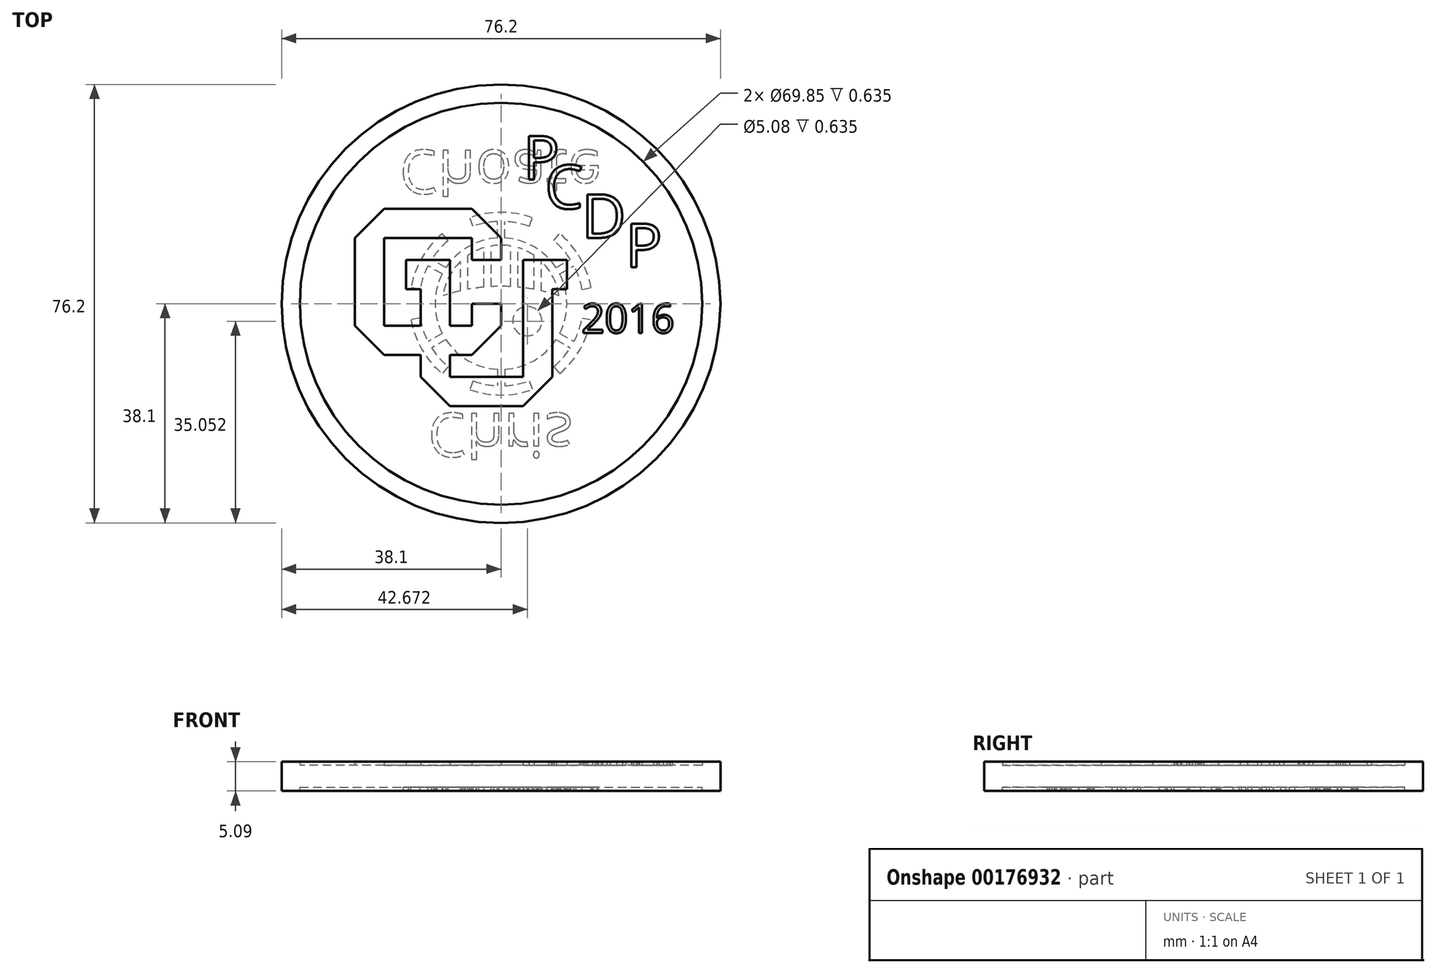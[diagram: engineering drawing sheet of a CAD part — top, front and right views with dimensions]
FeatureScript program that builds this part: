
annotation { "Feature Type Name" : "Feature", "Feature Type Description" : "" }
export const myFeature = defineFeature(function(context is Context, id is Id, definition is map)
    precondition{}
    {
        {
            var Q0;
            Q0=qCreatedBy(makeId("Top.planeOp"),FACE);
            var sketch = newSketch(context, id + "F0", { "sketchPlane" : qUnion([Q0])});
            skCircle(sketch, "E0", {"center": v(0, 0) * mm, "radius": 38.1 * mm});
            skSolve(sketch);
        }
        {
            var Q0;
            Q0=makeQuery(id+"F0.imprint","IMPRINT",FACE,{"disambiguationData":[TD([[makeQuery(id+"F0.imprint","IMPRINT",EDGE,{"derivedFrom":sQuery(id+"F0.wireOp",EDGE,"E0")}),1.0]])]});
            extrude(context, id + "F1", {"entities" : qUnion([Q0]), "depth" : 3.8 * mm});
        }
        {
            var Q0;
            Q0=makeQuery(id+"F1.opExtrude","CAP_FACE",FACE,{"disambiguationData":[OSD([sQuery(id+"F0.wireOp",EDGE,"E0")])],"isStart":false});
            var sketch = newSketch(context, id + "F2", { "sketchPlane" : qUnion([Q0])});
            skLineSegment(sketch, "E1", {"start": v(0, 0) * mm, "end": v(0, -3.81) * mm});
            skLineSegment(sketch, "E2", {"start": v(0, -3.81) * mm, "end": v(-5.08, -8.9) * mm});
            skLineSegment(sketch, "E3", {"start": v(-5.08, -8.9) * mm, "end": v(-8.9, -8.9) * mm});
            skLineSegment(sketch, "E4", {"start": v(-20.32, -8.9) * mm, "end": v(-25.4, -3.81) * mm});
            skLineSegment(sketch, "E5", {"start": v(-25.4, -3.81) * mm, "end": v(-25.4, 11.43) * mm});
            skLineSegment(sketch, "E6", {"start": v(-25.4, 11.43) * mm, "end": v(-20.32, 16.5) * mm});
            skLineSegment(sketch, "E7", {"start": v(-20.32, 16.51) * mm, "end": v(-5.08, 16.51) * mm});
            skLineSegment(sketch, "E8", {"start": v(-5.08, 16.51) * mm, "end": v(0, 11.43) * mm});
            skLineSegment(sketch, "E9", {"start": v(0, 11.43) * mm, "end": v(0, 7.62) * mm});
            skLineSegment(sketch, "E10", {"start": v(0, 7.62) * mm, "end": v(-5.08, 7.62) * mm});
            skLineSegment(sketch, "E11", {"start": v(-5.08, 7.62) * mm, "end": v(-5.08, 11.43) * mm});
            skLineSegment(sketch, "E12", {"start": v(-5.08, 11.43) * mm, "end": v(-20.32, 11.43) * mm});
            skLineSegment(sketch, "E13", {"start": v(-20.32, 11.43) * mm, "end": v(-20.32, -3.81) * mm});
            skLineSegment(sketch, "E14", {"start": v(-20.32, -3.81) * mm, "end": v(-13.97, -3.81) * mm});
            skLineSegment(sketch, "E15", {"start": v(-5.08, -3.81) * mm, "end": v(-5.08, 0) * mm});
            skLineSegment(sketch, "E16", {"start": v(-5.08, 0) * mm, "end": v(0, 0) * mm});
            skLineSegment(sketch, "E17", {"start": v(-8.9, -3.81) * mm, "end": v(-8.9, 7.62) * mm});
            skLineSegment(sketch, "E18", {"start": v(-8.9, 7.62) * mm, "end": v(-16.5, 7.62) * mm});
            skLineSegment(sketch, "E19", {"start": v(-16.5, 7.62) * mm, "end": v(-16.5, 2.54) * mm});
            skLineSegment(sketch, "E20", {"start": v(-16.51, 2.54) * mm, "end": v(-13.97, 2.54) * mm});
            skLineSegment(sketch, "E21", {"start": v(-13.97, 2.54) * mm, "end": v(-13.97, -3.8) * mm});
            skLineSegment(sketch, "E22.trimOffspring", {"start": v(-8.9, -3.81) * mm, "end": v(-5.08, -3.81) * mm});
            skLineSegment(sketch, "E23", {"start": v(-13.97, -12.7) * mm, "end": v(-13.97, -8.9) * mm});
            skLineSegment(sketch, "E24", {"start": v(-13.97, -12.7) * mm, "end": v(-8.9, -17.78) * mm});
            skLineSegment(sketch, "E25", {"start": v(-8.9, -17.78) * mm, "end": v(3.8, -17.78) * mm});
            skLineSegment(sketch, "E26", {"start": v(3.8, -17.78) * mm, "end": v(8.89, -12.7) * mm});
            skLineSegment(sketch, "E27", {"start": v(8.89, -12.7) * mm, "end": v(8.9, 2.54) * mm});
            skLineSegment(sketch, "E28", {"start": v(8.9, 2.54) * mm, "end": v(11.43, 2.54) * mm});
            skLineSegment(sketch, "E29", {"start": v(11.43, 2.54) * mm, "end": v(11.43, 7.62) * mm});
            skLineSegment(sketch, "E30", {"start": v(11.43, 7.62) * mm, "end": v(3.8, 7.62) * mm});
            skLineSegment(sketch, "E31", {"start": v(3.8, 7.62) * mm, "end": v(3.8, -12.7) * mm});
            skLineSegment(sketch, "E32", {"start": v(3.8, -12.7) * mm, "end": v(-8.9, -12.7) * mm});
            skLineSegment(sketch, "E33", {"start": v(-8.9, -12.7) * mm, "end": v(-8.9, -8.9) * mm});
            skLineSegment(sketch, "E34.trimOffspring", {"start": v(-13.97, -8.9) * mm, "end": v(-20.32, -8.9) * mm});
            skCircle(sketch, "E35", {"center": v(0, 0) * mm, "radius": 38.1 * mm});
            skCircle(sketch, "E36.0", {"center": v(0, 0) * mm, "radius": 34.93 * mm});
            skText(sketch, "E37", { "text": "P\n", "fontName": "OpenSans-Regular.ttf"});
            skText(sketch, "E38", { "text": "C\n", "fontName": "OpenSans-Regular.ttf"});
            skText(sketch, "E39", { "text": "D\n", "fontName": "OpenSans-Regular.ttf"});
            skText(sketch, "E40", { "text": "P\n", "fontName": "OpenSans-Regular.ttf"});
            skText(sketch, "E41", { "text": "2016\n", "fontName": "OpenSans-Regular.ttf"});
            const initialGuessF2  = {"E37": [0.0038, 0.0216, 1, 0, 0.00762], "E38": [0.00762, 0.01651, 1, 0, 0.00762], "E39": [0.01397, 0.01143, 1, 0, 0.00762], "E40": [0.0216, 0.00635, 1, 0, 0.00762], "E41": [0.01397, -0.00508, 1, 0, 0.00508]};
            skSetInitialGuess(sketch, initialGuessF2);
            skSolve(sketch);
        }
        {
            var Q0;
            Q0 = qSketchRegion(id + "F2", true);
            var Q1;
            Q1=makeQuery(id+"F2.imprint","IMPRINT",FACE,{"disambiguationData":[TD([[makeQuery(id+"F2.imprint","IMPRINT",EDGE,{"derivedFrom":sQuery(id+"F2.wireOp",EDGE,"E37.sketch_text.stroke-0")}),-1.0]])]});
            var Q2;
            Q2=makeQuery(id+"F2.imprint","IMPRINT",FACE,{"disambiguationData":[TD([[makeQuery(id+"F2.imprint","IMPRINT",EDGE,{"derivedFrom":sQuery(id+"F2.wireOp",EDGE,"E38.sketch_text.stroke-0")}),-1.0]])]});
            var Q3;
            Q3=makeQuery(id+"F2.imprint","IMPRINT",FACE,{"disambiguationData":[TD([[makeQuery(id+"F2.imprint","IMPRINT",EDGE,{"derivedFrom":sQuery(id+"F2.wireOp",EDGE,"E39.sketch_text.stroke-0")}),-1.0]])]});
            var Q4;
            Q4=makeQuery(id+"F2.imprint","IMPRINT",FACE,{"disambiguationData":[TD([[makeQuery(id+"F2.imprint","IMPRINT",EDGE,{"derivedFrom":sQuery(id+"F2.wireOp",EDGE,"E40.sketch_text.stroke-0")}),-1.0]])]});
            var Q5;
            Q5=makeQuery(id+"F2.imprint","IMPRINT",FACE,{"disambiguationData":[TD([[makeQuery(id+"F2.imprint","IMPRINT",EDGE,{"derivedFrom":sQuery(id+"F2.wireOp",EDGE,"E1")}),-1.0]])]});
            var Q6;
            Q6=makeQuery(id+"F2.imprint","IMPRINT",FACE,{"disambiguationData":[TD([[makeQuery(id+"F2.imprint","IMPRINT",EDGE,{"derivedFrom":sQuery(id+"F2.wireOp",EDGE,"E41.sketch_text.stroke-0")}),-1.0]])]});
            var Q7;
            Q7=makeQuery(id+"F2.imprint","IMPRINT",FACE,{"disambiguationData":[TD([[makeQuery(id+"F2.imprint","IMPRINT",EDGE,{"derivedFrom":sQuery(id+"F2.wireOp",EDGE,"E41.sketch_text.stroke-20")}),-1.0]])]});
            var Q8;
            Q8=makeQuery(id+"F2.imprint","IMPRINT",FACE,{"disambiguationData":[TD([[makeQuery(id+"F2.imprint","IMPRINT",EDGE,{"derivedFrom":sQuery(id+"F2.wireOp",EDGE,"E41.sketch_text.stroke-36")}),-1.0]])]});
            var Q9;
            Q9=makeQuery(id+"F2.imprint","IMPRINT",FACE,{"disambiguationData":[TD([[makeQuery(id+"F2.imprint","IMPRINT",EDGE,{"derivedFrom":sQuery(id+"F2.wireOp",EDGE,"E41.sketch_text.stroke-45")}),-1.0]])]});
            extrude(context, id + "F3", {"entities" : qUnion([Q0, Q1, Q2, Q3, Q4, Q5, Q6, Q7, Q8, Q9]), "operationType" : NewBodyOperationType.ADD, "depth" : 0.64 * mm});
        }
        {
            var Q0;
            Q0=makeQuery(id+"F1.opExtrude","CAP_FACE",FACE,{"disambiguationData":[OSD([sQuery(id+"F0.wireOp",EDGE,"E0")])],"isStart":true});
            var sketch = newSketch(context, id + "F4", { "sketchPlane" : qUnion([Q0])});
            skCircle(sketch, "E42", {"center": v(0, 0) * mm, "radius": 38.1 * mm});
            skCircle(sketch, "E43", {"center": v(0, 0) * mm, "radius": 34.93 * mm});
            skText(sketch, "E44", { "text": "Chris\n", "fontName": "OpenSans-Regular.ttf"});
            skText(sketch, "E45", { "text": "Choate", "fontName": "OpenSans-Regular.ttf"});
            skArc(sketch, "E46", {"start": v(5.43, 14.92) * mm, "mid": v(0, 15.88) * mm, "end": v(-5.43, 14.92) * mm});
            skArc(sketch, "E47", {"start": v(4.89, 13.43) * mm, "mid": v(2.8, 14.01) * mm, "end": v(0.63, 14.27) * mm});
            skLineSegment(sketch, "E48", {"start": v(-4.89, 13.43) * mm, "end": v(-5.43, 14.92) * mm});
            skLineSegment(sketch, "E49.1.16.0", {"start": v(4.89, 13.43) * mm, "end": v(5.43, 14.92) * mm});
            skLineSegment(sketch, "E50", {"start": v(0.63, 11.41) * mm, "end": v(0.63, 14.27) * mm});
            skLineSegment(sketch, "E51", {"start": v(-0.64, 11.41) * mm, "end": v(-0.64, 14.27) * mm});
            skArc(sketch, "E52.trimOffspring", {"start": v(-0.64, 14.27) * mm, "mid": v(-2.8, 14.01) * mm, "end": v(-4.89, 13.43) * mm});
            skArc(sketch, "E53", {"start": v(-0.64, 11.41) * mm, "mid": v(-5.72, 9.9) * mm, "end": v(-9.57, 6.26) * mm});
            skLineSegment(sketch, "E54.1.0", {"start": v(-9.57, 6.26) * mm, "end": v(-12.04, 7.69) * mm});
            skLineSegment(sketch, "E54.1.1", {"start": v(-10.2, 5.16) * mm, "end": v(-12.68, 6.59) * mm});
            skArc(sketch, "E54.1.2", {"start": v(-12.68, 6.59) * mm, "mid": v(-13.53, 4.59) * mm, "end": v(-14.07, 2.48) * mm});
            skLineSegment(sketch, "E54.1.3", {"start": v(-14.07, 2.48) * mm, "end": v(-15.63, 2.76) * mm});
            skArc(sketch, "E54.1.4", {"start": v(-10.2, 12.16) * mm, "mid": v(-13.75, 7.94) * mm, "end": v(-15.63, 2.76) * mm});
            skLineSegment(sketch, "E54.1.5", {"start": v(-9.18, 10.94) * mm, "end": v(-10.2, 12.16) * mm});
            skArc(sketch, "E54.1.6", {"start": v(-9.18, 10.94) * mm, "mid": v(-10.74, 9.42) * mm, "end": v(-12.04, 7.69) * mm});
            skLineSegment(sketch, "E54.2.0", {"start": v(-10.2, -5.16) * mm, "end": v(-12.68, -6.59) * mm});
            skLineSegment(sketch, "E54.2.1", {"start": v(-9.57, -6.26) * mm, "end": v(-12.04, -7.69) * mm});
            skArc(sketch, "E54.2.2", {"start": v(-12.04, -7.69) * mm, "mid": v(-10.74, -9.42) * mm, "end": v(-9.18, -10.94) * mm});
            skLineSegment(sketch, "E54.2.3", {"start": v(-9.18, -10.94) * mm, "end": v(-10.2, -12.16) * mm});
            skArc(sketch, "E54.2.4", {"start": v(-15.63, -2.76) * mm, "mid": v(-13.75, -7.94) * mm, "end": v(-10.2, -12.16) * mm});
            skLineSegment(sketch, "E54.2.5", {"start": v(-14.07, -2.48) * mm, "end": v(-15.63, -2.76) * mm});
            skArc(sketch, "E54.2.6", {"start": v(-14.07, -2.48) * mm, "mid": v(-13.53, -4.59) * mm, "end": v(-12.68, -6.59) * mm});
            skLineSegment(sketch, "E55.1.3.0", {"start": v(-0.64, -11.41) * mm, "end": v(-0.64, -14.27) * mm});
            skLineSegment(sketch, "E55.3.3.0", {"start": v(0.64, -11.41) * mm, "end": v(0.63, -14.27) * mm});
            skArc(sketch, "E55.6.3.0", {"start": v(0.64, -14.27) * mm, "mid": v(2.8, -14.01) * mm, "end": v(4.89, -13.43) * mm});
            skLineSegment(sketch, "E55.10.3.0", {"start": v(4.89, -13.43) * mm, "end": v(5.43, -14.92) * mm});
            skArc(sketch, "E55.13.3.0", {"start": v(-5.43, -14.92) * mm, "mid": v(0, -15.88) * mm, "end": v(5.43, -14.92) * mm});
            skLineSegment(sketch, "E55.17.3.0", {"start": v(-4.89, -13.43) * mm, "end": v(-5.43, -14.92) * mm});
            skArc(sketch, "E55.20.3.0", {"start": v(-4.89, -13.43) * mm, "mid": v(-2.8, -14.01) * mm, "end": v(-0.64, -14.27) * mm});
            skLineSegment(sketch, "E55.1.4.0", {"start": v(9.57, -6.26) * mm, "end": v(12.04, -7.69) * mm});
            skLineSegment(sketch, "E55.3.4.0", {"start": v(10.2, -5.16) * mm, "end": v(12.68, -6.59) * mm});
            skArc(sketch, "E55.6.4.0", {"start": v(12.68, -6.59) * mm, "mid": v(13.53, -4.59) * mm, "end": v(14.07, -2.48) * mm});
            skLineSegment(sketch, "E55.10.4.0", {"start": v(14.07, -2.48) * mm, "end": v(15.63, -2.76) * mm});
            skArc(sketch, "E55.13.4.0", {"start": v(10.2, -12.16) * mm, "mid": v(13.75, -7.94) * mm, "end": v(15.63, -2.76) * mm});
            skLineSegment(sketch, "E55.17.4.0", {"start": v(9.18, -10.94) * mm, "end": v(10.2, -12.16) * mm});
            skArc(sketch, "E55.20.4.0", {"start": v(9.18, -10.94) * mm, "mid": v(10.74, -9.42) * mm, "end": v(12.04, -7.69) * mm});
            skLineSegment(sketch, "E55.1.5.0", {"start": v(10.2, 5.16) * mm, "end": v(12.68, 6.59) * mm});
            skLineSegment(sketch, "E55.3.5.0", {"start": v(9.57, 6.26) * mm, "end": v(12.04, 7.69) * mm});
            skArc(sketch, "E55.6.5.0", {"start": v(12.04, 7.69) * mm, "mid": v(10.74, 9.42) * mm, "end": v(9.18, 10.94) * mm});
            skLineSegment(sketch, "E55.10.5.0", {"start": v(9.18, 10.94) * mm, "end": v(10.2, 12.16) * mm});
            skArc(sketch, "E55.13.5.0", {"start": v(15.63, 2.76) * mm, "mid": v(13.75, 7.94) * mm, "end": v(10.2, 12.16) * mm});
            skLineSegment(sketch, "E55.17.5.0", {"start": v(14.07, 2.48) * mm, "end": v(15.63, 2.76) * mm});
            skArc(sketch, "E55.20.5.0", {"start": v(14.07, 2.48) * mm, "mid": v(13.53, 4.59) * mm, "end": v(12.68, 6.59) * mm});
            skArc(sketch, "E56.trimOffspring", {"start": v(-10.2, 5.16) * mm, "mid": v(-11.43, 0) * mm, "end": v(-10.2, -5.16) * mm});
            skArc(sketch, "E57.trimOffspring", {"start": v(-9.57, -6.26) * mm, "mid": v(-5.72, -9.9) * mm, "end": v(-0.63, -11.41) * mm});
            skArc(sketch, "E58.trimOffspring", {"start": v(0.64, -11.41) * mm, "mid": v(5.71, -9.9) * mm, "end": v(9.57, -6.26) * mm});
            skArc(sketch, "E59.trimOffspring", {"start": v(10.2, -5.16) * mm, "mid": v(11.43, 0) * mm, "end": v(10.2, 5.16) * mm});
            skArc(sketch, "E60.trimOffspring", {"start": v(9.57, 6.26) * mm, "mid": v(5.71, 9.9) * mm, "end": v(0.63, 11.41) * mm});
            skCircle(sketch, "E61", {"center": v(0, 0) * mm, "radius": 0.63 * mm});
            skCircle(sketch, "E62", {"center": v(-4.57, 3.05) * mm, "radius": 2.54 * mm});
            skCircle(sketch, "E63.MirrorC", {"center": v(4.57, 3.05) * mm, "radius": 2.54 * mm});
            skArc(sketch, "E64", {"start": v(-10.07, -1.38) * mm, "mid": v(-9.05, -4.62) * mm, "end": v(-7.02, -7.35) * mm});
            skArc(sketch, "E65", {"start": v(-10.16, 0) * mm, "mid": v(0, -1.74) * mm, "end": v(10.16, 0) * mm});
            skArc(sketch, "E66.0", {"start": v(-10.07, -1.38) * mm, "mid": v(-8.55, -1.84) * mm, "end": v(-7.02, -2.23) * mm});
            skArc(sketch, "E67.trimOffspring", {"start": v(10.16, 0) * mm, "mid": v(0, 10.16) * mm, "end": v(-10.16, 0) * mm});
            skLineSegment(sketch, "E68", {"start": v(-5.75, -2.49) * mm, "end": v(-5.75, -8.38) * mm});
            skLineSegment(sketch, "E69", {"start": v(-7.02, -2.23) * mm, "end": v(-7.02, -7.35) * mm});
            skArc(sketch, "E70.trimOffspring", {"start": v(-5.75, -2.49) * mm, "mid": v(-4.36, -2.71) * mm, "end": v(-2.95, -2.88) * mm});
            skArc(sketch, "E71.trimOffspring", {"start": v(-5.75, -8.38) * mm, "mid": v(-4.4, -9.16) * mm, "end": v(-2.95, -9.72) * mm});
            skLineSegment(sketch, "E72", {"start": v(-1.68, -2.97) * mm, "end": v(-1.68, -10.02) * mm});
            skLineSegment(sketch, "E73", {"start": v(-2.95, -2.88) * mm, "end": v(-2.95, -9.72) * mm});
            skArc(sketch, "E74.trimOffspring", {"start": v(-1.68, -2.97) * mm, "mid": v(0, -3.01) * mm, "end": v(1.68, -2.97) * mm});
            skArc(sketch, "E75.trimOffspring", {"start": v(-1.68, -10.02) * mm, "mid": v(0, -10.16) * mm, "end": v(1.68, -10.02) * mm});
            skLineSegment(sketch, "E76.MirrorCS", {"start": v(1.68, -2.97) * mm, "end": v(1.68, -10.02) * mm});
            skLineSegment(sketch, "E77.MirrorCS", {"start": v(2.95, -2.88) * mm, "end": v(2.95, -9.72) * mm});
            skLineSegment(sketch, "E78.MirrorCS", {"start": v(5.75, -2.49) * mm, "end": v(5.75, -8.38) * mm});
            skLineSegment(sketch, "E79.MirrorCS", {"start": v(7.02, -2.23) * mm, "end": v(7.02, -7.35) * mm});
            skArc(sketch, "E80.trimOffspring", {"start": v(2.95, -2.88) * mm, "mid": v(4.36, -2.71) * mm, "end": v(5.75, -2.49) * mm});
            skArc(sketch, "E81.trimOffspring", {"start": v(2.95, -9.72) * mm, "mid": v(4.4, -9.16) * mm, "end": v(5.75, -8.38) * mm});
            skArc(sketch, "E82.trimOffspring", {"start": v(7.02, -7.35) * mm, "mid": v(9.05, -4.62) * mm, "end": v(10.07, -1.38) * mm});
            skArc(sketch, "E83.trimOffspring", {"start": v(7.02, -2.23) * mm, "mid": v(8.55, -1.84) * mm, "end": v(10.07, -1.38) * mm});
            const initialGuessF4  = {"E44": [-0.0127, 0.01905, 1, 0, 0.00762], "E45": [-0.01763, -0.02667, 1, 0, 0.00762]};
            skSetInitialGuess(sketch, initialGuessF4);
            skSolve(sketch);
        }
        {
            var Q0;
            Q0 = qSketchRegion(id + "F4", true);
            var Q1;
            Q1=makeQuery(id+"F4.imprint","IMPRINT",FACE,{"disambiguationData":[TD([[makeQuery(id+"F4.imprint","IMPRINT",EDGE,{"derivedFrom":sQuery(id+"F4.wireOp",EDGE,"E44.sketch_text.stroke-46")}),-1.0]])]});
            var Q2;
            Q2=makeQuery(id+"F4.imprint","IMPRINT",FACE,{"disambiguationData":[TD([[makeQuery(id+"F4.imprint","IMPRINT",EDGE,{"derivedFrom":sQuery(id+"F4.wireOp",EDGE,"E44.sketch_text.stroke-50")}),-1.0]])]});
            var Q3;
            Q3=makeQuery(id+"F4.imprint","IMPRINT",FACE,{"disambiguationData":[TD([[makeQuery(id+"F4.imprint","IMPRINT",EDGE,{"derivedFrom":sQuery(id+"F4.wireOp",EDGE,"E44.sketch_text.stroke-33")}),-1.0]])]});
            var Q4;
            Q4=makeQuery(id+"F4.imprint","IMPRINT",FACE,{"disambiguationData":[TD([[makeQuery(id+"F4.imprint","IMPRINT",EDGE,{"derivedFrom":sQuery(id+"F4.wireOp",EDGE,"E44.sketch_text.stroke-15")}),-1.0]])]});
            var Q5;
            Q5=makeQuery(id+"F4.imprint","IMPRINT",FACE,{"disambiguationData":[TD([[makeQuery(id+"F4.imprint","IMPRINT",EDGE,{"derivedFrom":sQuery(id+"F4.wireOp",EDGE,"E44.sketch_text.stroke-0")}),-1.0]])]});
            var Q6;
            Q6=makeQuery(id+"F4.imprint","IMPRINT",FACE,{"disambiguationData":[TD([[makeQuery(id+"F4.imprint","IMPRINT",EDGE,{"derivedFrom":sQuery(id+"F4.wireOp",EDGE,"E44.sketch_text.stroke-58")}),-1.0]])]});
            var Q7;
            Q7=makeQuery(id+"F4.imprint","IMPRINT",FACE,{"disambiguationData":[TD([[makeQuery(id+"F4.imprint","IMPRINT",EDGE,{"derivedFrom":sQuery(id+"F4.wireOp",EDGE,"E46")}),1.0]])]});
            var Q8;
            Q8=makeQuery(id+"F4.imprint","IMPRINT",FACE,{"disambiguationData":[TD([[makeQuery(id+"F4.imprint","IMPRINT",EDGE,{"derivedFrom":sQuery(id+"F4.wireOp",EDGE,"E63.MirrorC")}),-1.0]])]});
            var Q9;
            Q9=makeQuery(id+"F4.imprint","IMPRINT",FACE,{"disambiguationData":[TD([[makeQuery(id+"F4.imprint","IMPRINT",EDGE,{"derivedFrom":sQuery(id+"F4.wireOp",EDGE,"E62")}),1.0]])]});
            var Q10;
            Q10=makeQuery(id+"F4.imprint","IMPRINT",FACE,{"disambiguationData":[TD([[makeQuery(id+"F4.imprint","IMPRINT",EDGE,{"derivedFrom":sQuery(id+"F4.wireOp",EDGE,"E61")}),1.0]])]});
            var Q11;
            Q11=makeQuery(id+"F4.imprint","IMPRINT",FACE,{"disambiguationData":[TD([[makeQuery(id+"F4.imprint","IMPRINT",EDGE,{"derivedFrom":sQuery(id+"F4.wireOp",EDGE,"E45.sketch_text.stroke-0")}),-1.0]])]});
            var Q12;
            Q12=makeQuery(id+"F4.imprint","IMPRINT",FACE,{"disambiguationData":[TD([[makeQuery(id+"F4.imprint","IMPRINT",EDGE,{"derivedFrom":sQuery(id+"F4.wireOp",EDGE,"E45.sketch_text.stroke-15")}),-1.0]])]});
            var Q13;
            Q13=makeQuery(id+"F4.imprint","IMPRINT",FACE,{"disambiguationData":[TD([[makeQuery(id+"F4.imprint","IMPRINT",EDGE,{"derivedFrom":sQuery(id+"F4.wireOp",EDGE,"E45.sketch_text.stroke-33")}),-1.0]])]});
            var Q14;
            Q14=makeQuery(id+"F4.imprint","IMPRINT",FACE,{"disambiguationData":[TD([[makeQuery(id+"F4.imprint","IMPRINT",EDGE,{"derivedFrom":sQuery(id+"F4.wireOp",EDGE,"E45.sketch_text.stroke-50")}),-1.0]])]});
            var Q15;
            Q15=makeQuery(id+"F4.imprint","IMPRINT",FACE,{"disambiguationData":[TD([[makeQuery(id+"F4.imprint","IMPRINT",EDGE,{"derivedFrom":sQuery(id+"F4.wireOp",EDGE,"E45.sketch_text.stroke-77")}),-1.0]])]});
            var Q16;
            Q16=makeQuery(id+"F4.imprint","IMPRINT",FACE,{"disambiguationData":[TD([[makeQuery(id+"F4.imprint","IMPRINT",EDGE,{"derivedFrom":sQuery(id+"F4.wireOp",EDGE,"E45.sketch_text.stroke-96")}),-1.0]])]});
            extrude(context, id + "F5", {"entities" : qUnion([Q0, Q1, Q2, Q3, Q4, Q5, Q6, Q7, Q8, Q9, Q10, Q11, Q12, Q13, Q14, Q15, Q16]), "operationType" : NewBodyOperationType.ADD, "depth" : 0.64 * mm});
        }
    });
